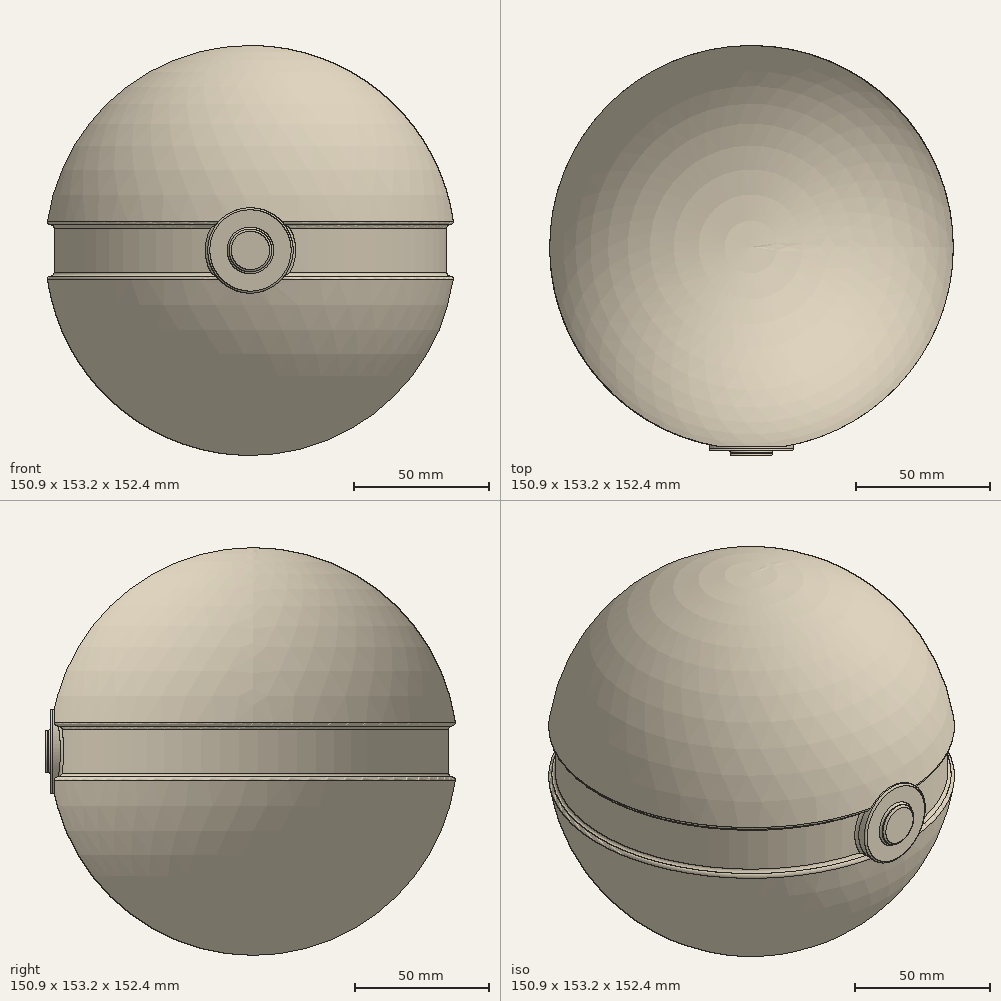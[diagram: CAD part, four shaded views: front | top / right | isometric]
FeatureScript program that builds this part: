
annotation { "Feature Type Name" : "Feature", "Feature Type Description" : "" }
export const myFeature = defineFeature(function(context is Context, id is Id, definition is map)
    precondition{}
    {
        {
            var Q0;
            Q0=qCreatedBy(makeId("Front.planeOp"),FACE);
            var sketch = newSketch(context, id + "F0", { "sketchPlane" : qUnion([Q0])});
            skArc(sketch, "E0", {"start": v(0, 76.2) * mm, "mid": v(-50.4, 57.15) * mm, "end": v(-75.6, 9.52) * mm});
            skLineSegment(sketch, "E1.bottom", {"start": v(-75.6, 9.53) * mm, "end": v(-73.03, 9.53) * mm});
            skLineSegment(sketch, "E1.top", {"start": v(-75.6, -9.53) * mm, "end": v(-73.03, -9.53) * mm});
            skLineSegment(sketch, "E2", {"start": v(0, 76.2) * mm, "end": v(0, -76.2) * mm});
            skLineSegment(sketch, "E3", {"start": v(-73.03, 9.53) * mm, "end": v(-73.03, -9.53) * mm});
            skArc(sketch, "E4.trimOffspring", {"start": v(-75.6, -9.53) * mm, "mid": v(-50.4, -57.15) * mm, "end": v(0, -76.2) * mm});
            skSolve(sketch);
        }
        {
            var Q0;
            Q0=makeQuery(id+"F0.imprint","IMPRINT",FACE,{"disambiguationData":[TD([[makeQuery(id+"F0.imprint","IMPRINT",EDGE,{"derivedFrom":sQuery(id+"F0.wireOp",EDGE,"E0")}),1.0]])]});
            var Q1;
            Q1=sQuery(id+"F0.wireOp",EDGE,"E2");
            revolve(context, id + "F1", {"entities" : qUnion([Q0]), "axis" : qUnion([Q1]), "revolveType" : RevolveType.FULL});
        }
        {
            var Q0;
            Q0=qCreatedBy(makeId("Front.planeOp"),FACE);
            cPlane(context, id + "F2", {"entities" : qUnion([Q0]), "cplaneType" : CPlaneType.OFFSET, "offset" : 76.2 * mm, "width" : 152.4 * mm, "height" : 152.4 * mm});
        }
        {
            var Q0;
            Q0=qCreatedBy(id+"F2.planeOp",FACE);
            var sketch = newSketch(context, id + "F3", { "sketchPlane" : qUnion([Q0])});
            skCircle(sketch, "E5", {"center": v(0, 0) * mm, "radius": 15.88 * mm});
            skSolve(sketch);
        }
        {
            var Q0;
            Q0=makeQuery(id+"F3.imprint","IMPRINT",FACE,{"disambiguationData":[TD([[makeQuery(id+"F3.imprint","IMPRINT",EDGE,{"derivedFrom":sQuery(id+"F3.wireOp",EDGE,"E5")}),1.0]])]});
            extrude(context, id + "F4", {"entities" : qUnion([Q0]), "operationType" : NewBodyOperationType.ADD, "depth" : 1.59 * mm, "hasSecondDirection" : true, "secondDirectionOppositeDirection" : true, "secondDirectionDepth" : 12.7 * mm});
        }
        {
            var Q0;
            Q0=makeQuery(id+"F4.opExtrude","CAP_FACE",FACE,{"disambiguationData":[OSD([sQuery(id+"F3.wireOp",EDGE,"E5")])],"isStart":false});
            var sketch = newSketch(context, id + "F5", { "sketchPlane" : qUnion([Q0])});
            skCircle(sketch, "E6", {"center": v(0, 0) * mm, "radius": 7.94 * mm});
            skSolve(sketch);
        }
        {
            var Q0;
            Q0=makeQuery(id+"F5.imprint","IMPRINT",FACE,{"disambiguationData":[TD([[makeQuery(id+"F5.imprint","IMPRINT",EDGE,{"derivedFrom":sQuery(id+"F5.wireOp",EDGE,"E6")}),-1.0]])]});
            extrude(context, id + "F6", {"entities" : qUnion([Q0]), "operationType" : NewBodyOperationType.REMOVE, "oppositeDirection" : true, "depth" : 1.9 * mm});
        }
        {
            var Q0;
            Q0=makeQuery(id+"F1.opRevolve","SWEPT_EDGE",EDGE,{"disambiguationData":[OSD([sQuery(id+"F0.wireOp",EDGE,"E1.bottom"),sQuery(id+"F0.wireOp",EDGE,"E3")])]});
            var Q1;
            Q1=makeQuery(id+"F1.opRevolve","SWEPT_EDGE",EDGE,{"disambiguationData":[OSD([sQuery(id+"F0.wireOp",EDGE,"E0"),sQuery(id+"F0.wireOp",EDGE,"E1.bottom")])]});
            var Q2;
            Q2=makeQuery(id+"F1.opRevolve","SWEPT_EDGE",EDGE,{"disambiguationData":[OSD([sQuery(id+"F0.wireOp",EDGE,"E1.top"),sQuery(id+"F0.wireOp",EDGE,"E3")])]});
            var Q3;
            Q3=makeQuery(id+"F1.opRevolve","SWEPT_EDGE",EDGE,{"disambiguationData":[OSD([sQuery(id+"F0.wireOp",EDGE,"E1.top"),sQuery(id+"F0.wireOp",EDGE,"E4.trimOffspring")])]});
            var Q4;
            Q4=makeQuery(id+"F4.boolean.opBoolean","INTERSECT",EDGE,{"disambiguationData":[OD(1.0)],"derivedFrom":[makeQuery(id+"F1.opRevolve","SWEPT_FACE",FACE,{"disambiguationData":[OSD([sQuery(id+"F0.wireOp",EDGE,"E3")])]}),makeQuery(id+"F4.opExtrude","SWEPT_FACE",FACE,{"disambiguationData":[OSD([sQuery(id+"F3.wireOp",EDGE,"E5")])]})]});
            var Q5;
            Q5=makeQuery(id+"F4.boolean.opBoolean","INTERSECT",EDGE,{"disambiguationData":[OD(0.0)],"derivedFrom":[makeQuery(id+"F1.opRevolve","SWEPT_FACE",FACE,{"disambiguationData":[OSD([sQuery(id+"F0.wireOp",EDGE,"E3")])]}),makeQuery(id+"F4.opExtrude","SWEPT_FACE",FACE,{"disambiguationData":[OSD([sQuery(id+"F3.wireOp",EDGE,"E5")])]})]});
            fillet(context, id + "F7", {"entities" : qUnion([Q0, Q1, Q2, Q3, Q4, Q5]), "radius" : 1.2 * mm, "tangentPropagation" : true, "allowEdgeOverflow" : false});
        }
        {
            var Q0;
            Q0=makeQuery(id+"F6.boolean.opBoolean","COPY",FACE,{"derivedFrom":makeQuery(id+"F6.opExtrude","CAP_FACE",FACE,{"disambiguationData":[OSD([sQuery(id+"F3.wireOp",EDGE,"E5"),sQuery(id+"F5.wireOp",EDGE,"E6")])],"isStart":false})});
            var Q1;
            Q1=makeQuery(id+"F4.opExtrude","CAP_FACE",FACE,{"disambiguationData":[OSD([sQuery(id+"F3.wireOp",EDGE,"E5")])],"isStart":false});
            fillet(context, id + "F8", {"entities" : qUnion([Q0, Q1]), "radius" : 0.76 * mm, "tangentPropagation" : true, "allowEdgeOverflow" : false});
        }
    });
